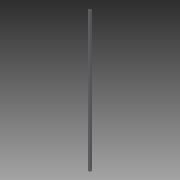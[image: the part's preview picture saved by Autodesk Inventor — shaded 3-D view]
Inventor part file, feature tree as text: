
AUTODESK INVENTOR PART (.ipt)
format: ipt  version: 2015 SP1 (Build 190203100, 203)  size: 93,696 bytes
history: native  units: mm
features: extrude x3, sketch x3
ambient origin geometry x8: Origin, YZ Plane, XZ Plane, XY Plane, X Axis, Y Axis, Z Axis, Center Point
bodies: Solid1 (feature_tree)
feature tree (6):
  extrude  "Extrusion1"  Depth=25.0mm
  extrude  "Extrusion2"  Depth=1.0mm TaperAngle=0.0deg
  extrude  "Extrusion3"  Depth=20.0mm
  sketch  "Sketch1"  dims[d0=25.0mm d1=25.0mm]
  sketch  "Sketch2"  dims[d2=1.0mm d3=1678.0mm d4=0.0mm]
  sketch  "Sketch3"  dims[d5=20.0mm d6=20.0mm d7=1000.0mm d8=0.0mm d9=3.141593mm d10=1000.0mm d11=0.0mm]
